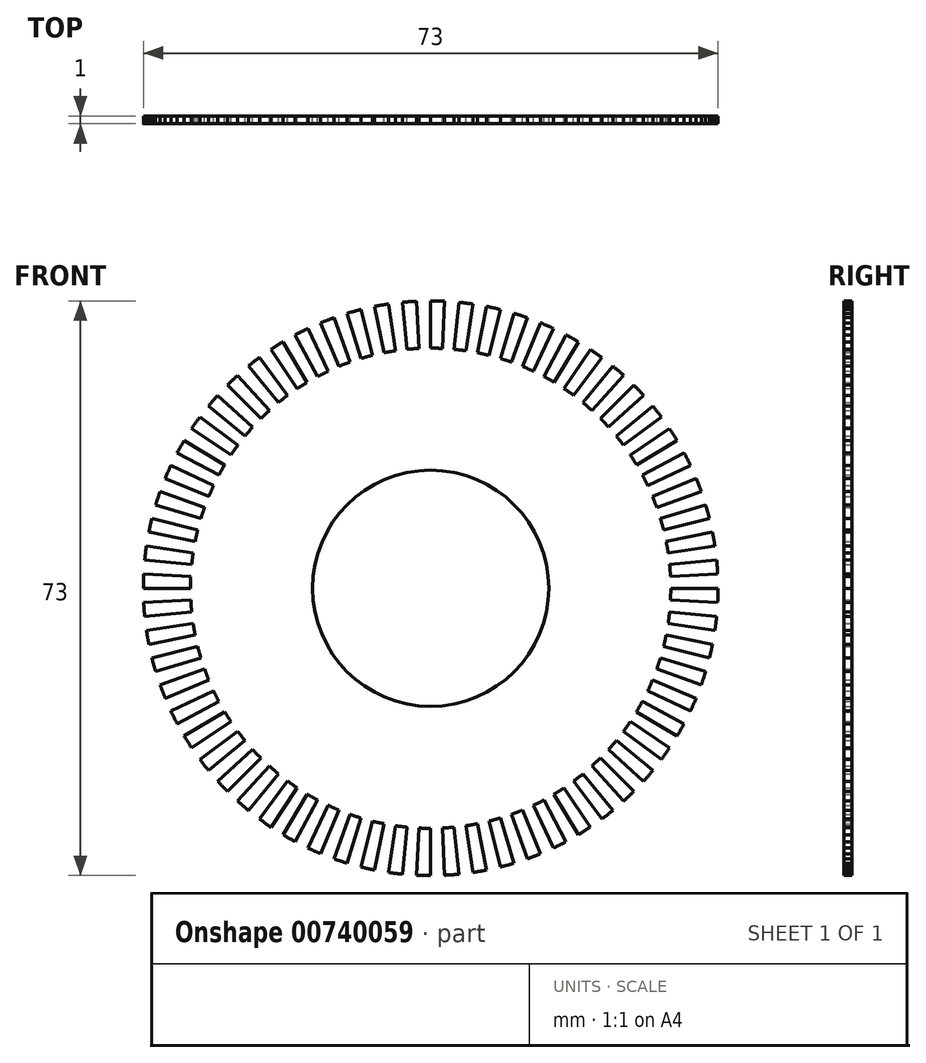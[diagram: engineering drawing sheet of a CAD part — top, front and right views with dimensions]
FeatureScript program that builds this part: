
annotation { "Feature Type Name" : "Feature", "Feature Type Description" : "" }
export const myFeature = defineFeature(function(context is Context, id is Id, definition is map)
    precondition{}
    {
        {
            var Q0;
            Q0=qCreatedBy(makeId("Front.planeOp"),FACE);
            var sketch = newSketch(context, id + "F0", { "sketchPlane" : qUnion([Q0])});
            skArc(sketch, "E0", {"start": v(1.8, 36.46) * mm, "mid": v(0.9, 36.49) * mm, "end": v(0, 36.5) * mm});
            skLineSegment(sketch, "E1", {"start": v(0, 30.5) * mm, "end": v(0, 36.5) * mm});
            skArc(sketch, "E2", {"start": v(1.5, 30.46) * mm, "mid": v(0.75, 30.5) * mm, "end": v(0, 30.5) * mm});
            skLineSegment(sketch, "E3", {"start": v(1.5, 30.46) * mm, "end": v(1.8, 36.46) * mm});
            skLineSegment(sketch, "E4.1.0", {"start": v(-1.5, 30.46) * mm, "end": v(-1.8, 36.46) * mm});
            skArc(sketch, "E4.1.1", {"start": v(-1.8, 36.46) * mm, "mid": v(-2.69, 36.4) * mm, "end": v(-3.58, 36.32) * mm});
            skArc(sketch, "E4.1.2", {"start": v(-1.5, 30.46) * mm, "mid": v(-2.24, 30.42) * mm, "end": v(-2.99, 30.35) * mm});
            skLineSegment(sketch, "E4.1.3", {"start": v(-2.99, 30.35) * mm, "end": v(-3.58, 36.32) * mm});
            skLineSegment(sketch, "E4.2.0", {"start": v(-4.48, 30.17) * mm, "end": v(-5.36, 36.1) * mm});
            skArc(sketch, "E4.2.1", {"start": v(-5.36, 36.1) * mm, "mid": v(-6.24, 35.96) * mm, "end": v(-7.12, 35.8) * mm});
            skArc(sketch, "E4.2.2", {"start": v(-4.48, 30.17) * mm, "mid": v(-5.21, 30.05) * mm, "end": v(-5.95, 29.91) * mm});
            skLineSegment(sketch, "E4.2.3", {"start": v(-5.95, 29.91) * mm, "end": v(-7.12, 35.8) * mm});
            skLineSegment(sketch, "E4.3.0", {"start": v(-7.41, 29.59) * mm, "end": v(-8.87, 35.4) * mm});
            skArc(sketch, "E4.3.1", {"start": v(-8.87, 35.4) * mm, "mid": v(-9.74, 35.18) * mm, "end": v(-10.6, 34.93) * mm});
            skArc(sketch, "E4.3.2", {"start": v(-7.41, 29.59) * mm, "mid": v(-8.13, 29.4) * mm, "end": v(-8.85, 29.19) * mm});
            skLineSegment(sketch, "E4.3.3", {"start": v(-8.85, 29.19) * mm, "end": v(-10.6, 34.93) * mm});
            skLineSegment(sketch, "E4.4.0", {"start": v(-10.28, 28.72) * mm, "end": v(-12.3, 34.37) * mm});
            skArc(sketch, "E4.4.1", {"start": v(-12.3, 34.37) * mm, "mid": v(-13.14, 34.05) * mm, "end": v(-13.97, 33.72) * mm});
            skArc(sketch, "E4.4.2", {"start": v(-10.28, 28.72) * mm, "mid": v(-10.98, 28.46) * mm, "end": v(-11.67, 28.18) * mm});
            skLineSegment(sketch, "E4.4.3", {"start": v(-11.67, 28.18) * mm, "end": v(-13.97, 33.72) * mm});
            skLineSegment(sketch, "E4.5.0", {"start": v(-13.04, 27.57) * mm, "end": v(-15.6, 33) * mm});
            skArc(sketch, "E4.5.1", {"start": v(-15.6, 33) * mm, "mid": v(-16.41, 32.6) * mm, "end": v(-17.2, 32.2) * mm});
            skArc(sketch, "E4.5.2", {"start": v(-13.04, 27.57) * mm, "mid": v(-13.71, 27.24) * mm, "end": v(-14.38, 26.9) * mm});
            skLineSegment(sketch, "E4.5.3", {"start": v(-14.38, 26.9) * mm, "end": v(-17.2, 32.2) * mm});
            skLineSegment(sketch, "E4.6.0", {"start": v(-15.68, 26.16) * mm, "end": v(-18.76, 31.3) * mm});
            skArc(sketch, "E4.6.1", {"start": v(-18.76, 31.3) * mm, "mid": v(-19.53, 30.84) * mm, "end": v(-20.28, 30.35) * mm});
            skArc(sketch, "E4.6.2", {"start": v(-15.68, 26.16) * mm, "mid": v(-16.32, 25.77) * mm, "end": v(-16.94, 25.36) * mm});
            skLineSegment(sketch, "E4.6.3", {"start": v(-16.94, 25.36) * mm, "end": v(-20.28, 30.35) * mm});
            skLineSegment(sketch, "E4.7.0", {"start": v(-18.17, 24.5) * mm, "end": v(-21.74, 29.32) * mm});
            skArc(sketch, "E4.7.1", {"start": v(-21.74, 29.32) * mm, "mid": v(-22.46, 28.77) * mm, "end": v(-23.16, 28.21) * mm});
            skArc(sketch, "E4.7.2", {"start": v(-18.17, 24.5) * mm, "mid": v(-18.76, 24.04) * mm, "end": v(-19.35, 23.58) * mm});
            skLineSegment(sketch, "E4.7.3", {"start": v(-19.35, 23.58) * mm, "end": v(-23.16, 28.21) * mm});
            skLineSegment(sketch, "E4.8.0", {"start": v(-20.48, 22.6) * mm, "end": v(-24.51, 27.04) * mm});
            skArc(sketch, "E4.8.1", {"start": v(-24.51, 27.04) * mm, "mid": v(-25.17, 26.44) * mm, "end": v(-25.8, 25.8) * mm});
            skArc(sketch, "E4.8.2", {"start": v(-20.48, 22.6) * mm, "mid": v(-21.03, 22.09) * mm, "end": v(-21.57, 21.57) * mm});
            skLineSegment(sketch, "E4.8.3", {"start": v(-21.57, 21.57) * mm, "end": v(-25.8, 25.8) * mm});
            skLineSegment(sketch, "E4.9.0", {"start": v(-22.6, 20.48) * mm, "end": v(-27.04, 24.51) * mm});
            skArc(sketch, "E4.9.1", {"start": v(-27.04, 24.51) * mm, "mid": v(-27.64, 23.84) * mm, "end": v(-28.21, 23.16) * mm});
            skArc(sketch, "E4.9.2", {"start": v(-22.6, 20.48) * mm, "mid": v(-23.1, 19.92) * mm, "end": v(-23.58, 19.35) * mm});
            skLineSegment(sketch, "E4.9.3", {"start": v(-23.58, 19.35) * mm, "end": v(-28.21, 23.16) * mm});
            skLineSegment(sketch, "E4.10.0", {"start": v(-24.5, 18.17) * mm, "end": v(-29.32, 21.74) * mm});
            skArc(sketch, "E4.10.1", {"start": v(-29.32, 21.74) * mm, "mid": v(-29.84, 21.02) * mm, "end": v(-30.35, 20.28) * mm});
            skArc(sketch, "E4.10.2", {"start": v(-24.5, 18.17) * mm, "mid": v(-24.94, 17.56) * mm, "end": v(-25.36, 16.94) * mm});
            skLineSegment(sketch, "E4.10.3", {"start": v(-25.36, 16.94) * mm, "end": v(-30.35, 20.28) * mm});
            skLineSegment(sketch, "E4.11.0", {"start": v(-26.16, 15.68) * mm, "end": v(-31.3, 18.76) * mm});
            skArc(sketch, "E4.11.1", {"start": v(-31.3, 18.76) * mm, "mid": v(-31.76, 18) * mm, "end": v(-32.2, 17.2) * mm});
            skArc(sketch, "E4.11.2", {"start": v(-26.16, 15.68) * mm, "mid": v(-26.54, 15.03) * mm, "end": v(-26.9, 14.38) * mm});
            skLineSegment(sketch, "E4.11.3", {"start": v(-26.9, 14.38) * mm, "end": v(-32.2, 17.2) * mm});
            skLineSegment(sketch, "E4.12.0", {"start": v(-27.57, 13.04) * mm, "end": v(-33, 15.6) * mm});
            skArc(sketch, "E4.12.1", {"start": v(-33, 15.6) * mm, "mid": v(-33.37, 14.8) * mm, "end": v(-33.72, 13.97) * mm});
            skArc(sketch, "E4.12.2", {"start": v(-27.57, 13.04) * mm, "mid": v(-27.88, 12.36) * mm, "end": v(-28.18, 11.67) * mm});
            skLineSegment(sketch, "E4.12.3", {"start": v(-28.18, 11.67) * mm, "end": v(-33.72, 13.97) * mm});
            skLineSegment(sketch, "E4.13.0", {"start": v(-28.72, 10.28) * mm, "end": v(-34.37, 12.3) * mm});
            skArc(sketch, "E4.13.1", {"start": v(-34.37, 12.3) * mm, "mid": v(-34.66, 11.45) * mm, "end": v(-34.93, 10.6) * mm});
            skArc(sketch, "E4.13.2", {"start": v(-28.72, 10.28) * mm, "mid": v(-28.96, 9.57) * mm, "end": v(-29.19, 8.85) * mm});
            skLineSegment(sketch, "E4.13.3", {"start": v(-29.19, 8.85) * mm, "end": v(-34.93, 10.6) * mm});
            skLineSegment(sketch, "E4.14.0", {"start": v(-29.59, 7.41) * mm, "end": v(-35.4, 8.87) * mm});
            skArc(sketch, "E4.14.1", {"start": v(-35.4, 8.87) * mm, "mid": v(-35.61, 8) * mm, "end": v(-35.8, 7.12) * mm});
            skArc(sketch, "E4.14.2", {"start": v(-29.59, 7.41) * mm, "mid": v(-29.76, 6.68) * mm, "end": v(-29.91, 5.95) * mm});
            skLineSegment(sketch, "E4.14.3", {"start": v(-29.91, 5.95) * mm, "end": v(-35.8, 7.12) * mm});
            skLineSegment(sketch, "E4.15.0", {"start": v(-30.17, 4.48) * mm, "end": v(-36.1, 5.36) * mm});
            skArc(sketch, "E4.15.1", {"start": v(-36.1, 5.36) * mm, "mid": v(-36.23, 4.47) * mm, "end": v(-36.32, 3.58) * mm});
            skArc(sketch, "E4.15.2", {"start": v(-30.17, 4.48) * mm, "mid": v(-30.27, 3.73) * mm, "end": v(-30.35, 2.99) * mm});
            skLineSegment(sketch, "E4.15.3", {"start": v(-30.35, 2.99) * mm, "end": v(-36.32, 3.58) * mm});
            skLineSegment(sketch, "E4.16.0", {"start": v(-30.46, 1.5) * mm, "end": v(-36.46, 1.8) * mm});
            skArc(sketch, "E4.16.1", {"start": v(-36.46, 1.8) * mm, "mid": v(-36.49, 0.9) * mm, "end": v(-36.5, 0) * mm});
            skArc(sketch, "E4.16.2", {"start": v(-30.46, 1.5) * mm, "mid": v(-30.5, 0.75) * mm, "end": v(-30.5, 0) * mm});
            skLineSegment(sketch, "E4.16.3", {"start": v(-30.5, 0) * mm, "end": v(-36.5, 0) * mm});
            skLineSegment(sketch, "E4.17.0", {"start": v(-30.46, -1.5) * mm, "end": v(-36.46, -1.8) * mm});
            skArc(sketch, "E4.17.1", {"start": v(-36.46, -1.8) * mm, "mid": v(-36.4, -2.69) * mm, "end": v(-36.32, -3.58) * mm});
            skArc(sketch, "E4.17.2", {"start": v(-30.46, -1.5) * mm, "mid": v(-30.42, -2.24) * mm, "end": v(-30.35, -2.99) * mm});
            skLineSegment(sketch, "E4.17.3", {"start": v(-30.35, -2.99) * mm, "end": v(-36.32, -3.58) * mm});
            skLineSegment(sketch, "E4.18.0", {"start": v(-30.17, -4.48) * mm, "end": v(-36.1, -5.36) * mm});
            skArc(sketch, "E4.18.1", {"start": v(-36.1, -5.36) * mm, "mid": v(-35.96, -6.24) * mm, "end": v(-35.8, -7.12) * mm});
            skArc(sketch, "E4.18.2", {"start": v(-30.17, -4.48) * mm, "mid": v(-30.05, -5.21) * mm, "end": v(-29.91, -5.95) * mm});
            skLineSegment(sketch, "E4.18.3", {"start": v(-29.91, -5.95) * mm, "end": v(-35.8, -7.12) * mm});
            skLineSegment(sketch, "E4.19.0", {"start": v(-29.59, -7.41) * mm, "end": v(-35.4, -8.87) * mm});
            skArc(sketch, "E4.19.1", {"start": v(-35.4, -8.87) * mm, "mid": v(-35.18, -9.74) * mm, "end": v(-34.93, -10.6) * mm});
            skArc(sketch, "E4.19.2", {"start": v(-29.59, -7.41) * mm, "mid": v(-29.4, -8.13) * mm, "end": v(-29.19, -8.85) * mm});
            skLineSegment(sketch, "E4.19.3", {"start": v(-29.19, -8.85) * mm, "end": v(-34.93, -10.6) * mm});
            skLineSegment(sketch, "E4.20.0", {"start": v(-28.72, -10.28) * mm, "end": v(-34.37, -12.3) * mm});
            skArc(sketch, "E4.20.1", {"start": v(-34.37, -12.3) * mm, "mid": v(-34.05, -13.14) * mm, "end": v(-33.72, -13.97) * mm});
            skArc(sketch, "E4.20.2", {"start": v(-28.72, -10.28) * mm, "mid": v(-28.46, -10.98) * mm, "end": v(-28.18, -11.67) * mm});
            skLineSegment(sketch, "E4.20.3", {"start": v(-28.18, -11.67) * mm, "end": v(-33.72, -13.97) * mm});
            skLineSegment(sketch, "E4.21.0", {"start": v(-27.57, -13.04) * mm, "end": v(-33, -15.6) * mm});
            skArc(sketch, "E4.21.1", {"start": v(-33, -15.6) * mm, "mid": v(-32.6, -16.41) * mm, "end": v(-32.2, -17.2) * mm});
            skArc(sketch, "E4.21.2", {"start": v(-27.57, -13.04) * mm, "mid": v(-27.24, -13.71) * mm, "end": v(-26.9, -14.38) * mm});
            skLineSegment(sketch, "E4.21.3", {"start": v(-26.9, -14.38) * mm, "end": v(-32.2, -17.2) * mm});
            skLineSegment(sketch, "E4.22.0", {"start": v(-26.16, -15.68) * mm, "end": v(-31.3, -18.76) * mm});
            skArc(sketch, "E4.22.1", {"start": v(-31.3, -18.76) * mm, "mid": v(-30.84, -19.53) * mm, "end": v(-30.35, -20.28) * mm});
            skArc(sketch, "E4.22.2", {"start": v(-26.16, -15.68) * mm, "mid": v(-25.77, -16.32) * mm, "end": v(-25.36, -16.94) * mm});
            skLineSegment(sketch, "E4.22.3", {"start": v(-25.36, -16.94) * mm, "end": v(-30.35, -20.28) * mm});
            skLineSegment(sketch, "E4.23.0", {"start": v(-24.5, -18.17) * mm, "end": v(-29.32, -21.74) * mm});
            skArc(sketch, "E4.23.1", {"start": v(-29.32, -21.74) * mm, "mid": v(-28.77, -22.46) * mm, "end": v(-28.21, -23.16) * mm});
            skArc(sketch, "E4.23.2", {"start": v(-24.5, -18.17) * mm, "mid": v(-24.04, -18.76) * mm, "end": v(-23.58, -19.35) * mm});
            skLineSegment(sketch, "E4.23.3", {"start": v(-23.58, -19.35) * mm, "end": v(-28.21, -23.16) * mm});
            skLineSegment(sketch, "E4.24.0", {"start": v(-22.6, -20.48) * mm, "end": v(-27.04, -24.51) * mm});
            skArc(sketch, "E4.24.1", {"start": v(-27.04, -24.51) * mm, "mid": v(-26.44, -25.17) * mm, "end": v(-25.8, -25.8) * mm});
            skArc(sketch, "E4.24.2", {"start": v(-22.6, -20.48) * mm, "mid": v(-22.09, -21.03) * mm, "end": v(-21.57, -21.57) * mm});
            skLineSegment(sketch, "E4.24.3", {"start": v(-21.57, -21.57) * mm, "end": v(-25.8, -25.8) * mm});
            skLineSegment(sketch, "E4.25.0", {"start": v(-20.48, -22.6) * mm, "end": v(-24.51, -27.04) * mm});
            skArc(sketch, "E4.25.1", {"start": v(-24.51, -27.04) * mm, "mid": v(-23.84, -27.64) * mm, "end": v(-23.16, -28.21) * mm});
            skArc(sketch, "E4.25.2", {"start": v(-20.48, -22.6) * mm, "mid": v(-19.92, -23.1) * mm, "end": v(-19.35, -23.58) * mm});
            skLineSegment(sketch, "E4.25.3", {"start": v(-19.35, -23.58) * mm, "end": v(-23.16, -28.21) * mm});
            skLineSegment(sketch, "E4.26.0", {"start": v(-18.17, -24.5) * mm, "end": v(-21.74, -29.32) * mm});
            skArc(sketch, "E4.26.1", {"start": v(-21.74, -29.32) * mm, "mid": v(-21.02, -29.84) * mm, "end": v(-20.28, -30.35) * mm});
            skArc(sketch, "E4.26.2", {"start": v(-18.17, -24.5) * mm, "mid": v(-17.56, -24.94) * mm, "end": v(-16.94, -25.36) * mm});
            skLineSegment(sketch, "E4.26.3", {"start": v(-16.94, -25.36) * mm, "end": v(-20.28, -30.35) * mm});
            skLineSegment(sketch, "E4.27.0", {"start": v(-15.68, -26.16) * mm, "end": v(-18.76, -31.3) * mm});
            skArc(sketch, "E4.27.1", {"start": v(-18.76, -31.3) * mm, "mid": v(-18, -31.76) * mm, "end": v(-17.2, -32.2) * mm});
            skArc(sketch, "E4.27.2", {"start": v(-15.68, -26.16) * mm, "mid": v(-15.03, -26.54) * mm, "end": v(-14.38, -26.9) * mm});
            skLineSegment(sketch, "E4.27.3", {"start": v(-14.38, -26.9) * mm, "end": v(-17.2, -32.2) * mm});
            skLineSegment(sketch, "E4.28.0", {"start": v(-13.04, -27.57) * mm, "end": v(-15.6, -33) * mm});
            skArc(sketch, "E4.28.1", {"start": v(-15.6, -33) * mm, "mid": v(-14.8, -33.37) * mm, "end": v(-13.97, -33.72) * mm});
            skArc(sketch, "E4.28.2", {"start": v(-13.04, -27.57) * mm, "mid": v(-12.36, -27.88) * mm, "end": v(-11.67, -28.18) * mm});
            skLineSegment(sketch, "E4.28.3", {"start": v(-11.67, -28.18) * mm, "end": v(-13.97, -33.72) * mm});
            skLineSegment(sketch, "E4.29.0", {"start": v(-10.28, -28.72) * mm, "end": v(-12.3, -34.37) * mm});
            skArc(sketch, "E4.29.1", {"start": v(-12.3, -34.37) * mm, "mid": v(-11.45, -34.66) * mm, "end": v(-10.6, -34.93) * mm});
            skArc(sketch, "E4.29.2", {"start": v(-10.28, -28.72) * mm, "mid": v(-9.57, -28.96) * mm, "end": v(-8.85, -29.19) * mm});
            skLineSegment(sketch, "E4.29.3", {"start": v(-8.85, -29.19) * mm, "end": v(-10.6, -34.93) * mm});
            skLineSegment(sketch, "E4.30.0", {"start": v(-7.41, -29.59) * mm, "end": v(-8.87, -35.4) * mm});
            skArc(sketch, "E4.30.1", {"start": v(-8.87, -35.4) * mm, "mid": v(-8, -35.61) * mm, "end": v(-7.12, -35.8) * mm});
            skArc(sketch, "E4.30.2", {"start": v(-7.41, -29.59) * mm, "mid": v(-6.68, -29.76) * mm, "end": v(-5.95, -29.91) * mm});
            skLineSegment(sketch, "E4.30.3", {"start": v(-5.95, -29.91) * mm, "end": v(-7.12, -35.8) * mm});
            skLineSegment(sketch, "E4.31.0", {"start": v(-4.48, -30.17) * mm, "end": v(-5.36, -36.1) * mm});
            skArc(sketch, "E4.31.1", {"start": v(-5.36, -36.1) * mm, "mid": v(-4.47, -36.23) * mm, "end": v(-3.58, -36.32) * mm});
            skArc(sketch, "E4.31.2", {"start": v(-4.48, -30.17) * mm, "mid": v(-3.73, -30.27) * mm, "end": v(-2.99, -30.35) * mm});
            skLineSegment(sketch, "E4.31.3", {"start": v(-2.99, -30.35) * mm, "end": v(-3.58, -36.32) * mm});
            skLineSegment(sketch, "E4.32.0", {"start": v(-1.5, -30.46) * mm, "end": v(-1.8, -36.46) * mm});
            skArc(sketch, "E4.32.1", {"start": v(-1.8, -36.46) * mm, "mid": v(-0.9, -36.49) * mm, "end": v(0, -36.5) * mm});
            skArc(sketch, "E4.32.2", {"start": v(-1.5, -30.46) * mm, "mid": v(-0.75, -30.5) * mm, "end": v(0, -30.5) * mm});
            skLineSegment(sketch, "E4.32.3", {"start": v(0, -30.5) * mm, "end": v(0, -36.5) * mm});
            skLineSegment(sketch, "E4.33.0", {"start": v(1.5, -30.46) * mm, "end": v(1.8, -36.46) * mm});
            skArc(sketch, "E4.33.1", {"start": v(1.8, -36.46) * mm, "mid": v(2.69, -36.4) * mm, "end": v(3.58, -36.32) * mm});
            skArc(sketch, "E4.33.2", {"start": v(1.5, -30.46) * mm, "mid": v(2.24, -30.42) * mm, "end": v(2.99, -30.35) * mm});
            skLineSegment(sketch, "E4.33.3", {"start": v(2.99, -30.35) * mm, "end": v(3.58, -36.32) * mm});
            skLineSegment(sketch, "E4.34.0", {"start": v(4.48, -30.17) * mm, "end": v(5.36, -36.1) * mm});
            skArc(sketch, "E4.34.1", {"start": v(5.36, -36.1) * mm, "mid": v(6.24, -35.96) * mm, "end": v(7.12, -35.8) * mm});
            skArc(sketch, "E4.34.2", {"start": v(4.48, -30.17) * mm, "mid": v(5.21, -30.05) * mm, "end": v(5.95, -29.91) * mm});
            skLineSegment(sketch, "E4.34.3", {"start": v(5.95, -29.91) * mm, "end": v(7.12, -35.8) * mm});
            skLineSegment(sketch, "E4.35.0", {"start": v(7.41, -29.59) * mm, "end": v(8.87, -35.4) * mm});
            skArc(sketch, "E4.35.1", {"start": v(8.87, -35.4) * mm, "mid": v(9.74, -35.18) * mm, "end": v(10.6, -34.93) * mm});
            skArc(sketch, "E4.35.2", {"start": v(7.41, -29.59) * mm, "mid": v(8.13, -29.4) * mm, "end": v(8.85, -29.19) * mm});
            skLineSegment(sketch, "E4.35.3", {"start": v(8.85, -29.19) * mm, "end": v(10.6, -34.93) * mm});
            skLineSegment(sketch, "E4.36.0", {"start": v(10.28, -28.72) * mm, "end": v(12.3, -34.37) * mm});
            skArc(sketch, "E4.36.1", {"start": v(12.3, -34.37) * mm, "mid": v(13.14, -34.05) * mm, "end": v(13.97, -33.72) * mm});
            skArc(sketch, "E4.36.2", {"start": v(10.28, -28.72) * mm, "mid": v(10.98, -28.46) * mm, "end": v(11.67, -28.18) * mm});
            skLineSegment(sketch, "E4.36.3", {"start": v(11.67, -28.18) * mm, "end": v(13.97, -33.72) * mm});
            skLineSegment(sketch, "E4.37.0", {"start": v(13.04, -27.57) * mm, "end": v(15.6, -33) * mm});
            skArc(sketch, "E4.37.1", {"start": v(15.6, -33) * mm, "mid": v(16.41, -32.6) * mm, "end": v(17.2, -32.2) * mm});
            skArc(sketch, "E4.37.2", {"start": v(13.04, -27.57) * mm, "mid": v(13.71, -27.24) * mm, "end": v(14.38, -26.9) * mm});
            skLineSegment(sketch, "E4.37.3", {"start": v(14.38, -26.9) * mm, "end": v(17.2, -32.2) * mm});
            skLineSegment(sketch, "E4.38.0", {"start": v(15.68, -26.16) * mm, "end": v(18.76, -31.3) * mm});
            skArc(sketch, "E4.38.1", {"start": v(18.76, -31.3) * mm, "mid": v(19.53, -30.84) * mm, "end": v(20.28, -30.35) * mm});
            skArc(sketch, "E4.38.2", {"start": v(15.68, -26.16) * mm, "mid": v(16.32, -25.77) * mm, "end": v(16.94, -25.36) * mm});
            skLineSegment(sketch, "E4.38.3", {"start": v(16.94, -25.36) * mm, "end": v(20.28, -30.35) * mm});
            skLineSegment(sketch, "E4.39.0", {"start": v(18.17, -24.5) * mm, "end": v(21.74, -29.32) * mm});
            skArc(sketch, "E4.39.1", {"start": v(21.74, -29.32) * mm, "mid": v(22.46, -28.77) * mm, "end": v(23.16, -28.21) * mm});
            skArc(sketch, "E4.39.2", {"start": v(18.17, -24.5) * mm, "mid": v(18.76, -24.04) * mm, "end": v(19.35, -23.58) * mm});
            skLineSegment(sketch, "E4.39.3", {"start": v(19.35, -23.58) * mm, "end": v(23.16, -28.21) * mm});
            skLineSegment(sketch, "E4.40.0", {"start": v(20.48, -22.6) * mm, "end": v(24.51, -27.04) * mm});
            skArc(sketch, "E4.40.1", {"start": v(24.51, -27.04) * mm, "mid": v(25.17, -26.44) * mm, "end": v(25.8, -25.8) * mm});
            skArc(sketch, "E4.40.2", {"start": v(20.48, -22.6) * mm, "mid": v(21.03, -22.09) * mm, "end": v(21.57, -21.57) * mm});
            skLineSegment(sketch, "E4.40.3", {"start": v(21.57, -21.57) * mm, "end": v(25.8, -25.8) * mm});
            skLineSegment(sketch, "E4.41.0", {"start": v(22.6, -20.48) * mm, "end": v(27.04, -24.51) * mm});
            skArc(sketch, "E4.41.1", {"start": v(27.04, -24.51) * mm, "mid": v(27.64, -23.84) * mm, "end": v(28.21, -23.16) * mm});
            skArc(sketch, "E4.41.2", {"start": v(22.6, -20.48) * mm, "mid": v(23.1, -19.92) * mm, "end": v(23.58, -19.35) * mm});
            skLineSegment(sketch, "E4.41.3", {"start": v(23.58, -19.35) * mm, "end": v(28.21, -23.16) * mm});
            skLineSegment(sketch, "E4.42.0", {"start": v(24.5, -18.17) * mm, "end": v(29.32, -21.74) * mm});
            skArc(sketch, "E4.42.1", {"start": v(29.32, -21.74) * mm, "mid": v(29.84, -21.02) * mm, "end": v(30.35, -20.28) * mm});
            skArc(sketch, "E4.42.2", {"start": v(24.5, -18.17) * mm, "mid": v(24.94, -17.56) * mm, "end": v(25.36, -16.94) * mm});
            skLineSegment(sketch, "E4.42.3", {"start": v(25.36, -16.94) * mm, "end": v(30.35, -20.28) * mm});
            skLineSegment(sketch, "E4.43.0", {"start": v(26.16, -15.68) * mm, "end": v(31.3, -18.76) * mm});
            skArc(sketch, "E4.43.1", {"start": v(31.3, -18.76) * mm, "mid": v(31.76, -18) * mm, "end": v(32.2, -17.2) * mm});
            skArc(sketch, "E4.43.2", {"start": v(26.16, -15.68) * mm, "mid": v(26.54, -15.03) * mm, "end": v(26.9, -14.38) * mm});
            skLineSegment(sketch, "E4.43.3", {"start": v(26.9, -14.38) * mm, "end": v(32.2, -17.2) * mm});
            skLineSegment(sketch, "E4.44.0", {"start": v(27.57, -13.04) * mm, "end": v(33, -15.6) * mm});
            skArc(sketch, "E4.44.1", {"start": v(33, -15.6) * mm, "mid": v(33.37, -14.8) * mm, "end": v(33.72, -13.97) * mm});
            skArc(sketch, "E4.44.2", {"start": v(27.57, -13.04) * mm, "mid": v(27.88, -12.36) * mm, "end": v(28.18, -11.67) * mm});
            skLineSegment(sketch, "E4.44.3", {"start": v(28.18, -11.67) * mm, "end": v(33.72, -13.97) * mm});
            skLineSegment(sketch, "E4.45.0", {"start": v(28.72, -10.28) * mm, "end": v(34.37, -12.3) * mm});
            skArc(sketch, "E4.45.1", {"start": v(34.37, -12.3) * mm, "mid": v(34.66, -11.45) * mm, "end": v(34.93, -10.6) * mm});
            skArc(sketch, "E4.45.2", {"start": v(28.72, -10.28) * mm, "mid": v(28.96, -9.57) * mm, "end": v(29.19, -8.85) * mm});
            skLineSegment(sketch, "E4.45.3", {"start": v(29.19, -8.85) * mm, "end": v(34.93, -10.6) * mm});
            skLineSegment(sketch, "E4.46.0", {"start": v(29.59, -7.41) * mm, "end": v(35.4, -8.87) * mm});
            skArc(sketch, "E4.46.1", {"start": v(35.4, -8.87) * mm, "mid": v(35.61, -8) * mm, "end": v(35.8, -7.12) * mm});
            skArc(sketch, "E4.46.2", {"start": v(29.59, -7.41) * mm, "mid": v(29.76, -6.68) * mm, "end": v(29.91, -5.95) * mm});
            skLineSegment(sketch, "E4.46.3", {"start": v(29.91, -5.95) * mm, "end": v(35.8, -7.12) * mm});
            skLineSegment(sketch, "E4.47.0", {"start": v(30.17, -4.48) * mm, "end": v(36.1, -5.36) * mm});
            skArc(sketch, "E4.47.1", {"start": v(36.1, -5.36) * mm, "mid": v(36.23, -4.47) * mm, "end": v(36.32, -3.58) * mm});
            skArc(sketch, "E4.47.2", {"start": v(30.17, -4.48) * mm, "mid": v(30.27, -3.73) * mm, "end": v(30.35, -2.99) * mm});
            skLineSegment(sketch, "E4.47.3", {"start": v(30.35, -2.99) * mm, "end": v(36.32, -3.58) * mm});
            skLineSegment(sketch, "E4.48.0", {"start": v(30.46, -1.5) * mm, "end": v(36.46, -1.8) * mm});
            skArc(sketch, "E4.48.1", {"start": v(36.46, -1.8) * mm, "mid": v(36.49, -0.9) * mm, "end": v(36.5, 0) * mm});
            skArc(sketch, "E4.48.2", {"start": v(30.46, -1.5) * mm, "mid": v(30.5, -0.75) * mm, "end": v(30.5, 0) * mm});
            skLineSegment(sketch, "E4.48.3", {"start": v(30.5, 0) * mm, "end": v(36.5, 0) * mm});
            skLineSegment(sketch, "E4.49.0", {"start": v(30.46, 1.5) * mm, "end": v(36.46, 1.8) * mm});
            skArc(sketch, "E4.49.1", {"start": v(36.46, 1.8) * mm, "mid": v(36.4, 2.69) * mm, "end": v(36.32, 3.58) * mm});
            skArc(sketch, "E4.49.2", {"start": v(30.46, 1.5) * mm, "mid": v(30.42, 2.24) * mm, "end": v(30.35, 2.99) * mm});
            skLineSegment(sketch, "E4.49.3", {"start": v(30.35, 2.99) * mm, "end": v(36.32, 3.58) * mm});
            skLineSegment(sketch, "E4.50.0", {"start": v(30.17, 4.48) * mm, "end": v(36.1, 5.36) * mm});
            skArc(sketch, "E4.50.1", {"start": v(36.1, 5.36) * mm, "mid": v(35.96, 6.24) * mm, "end": v(35.8, 7.12) * mm});
            skArc(sketch, "E4.50.2", {"start": v(30.17, 4.48) * mm, "mid": v(30.05, 5.21) * mm, "end": v(29.91, 5.95) * mm});
            skLineSegment(sketch, "E4.50.3", {"start": v(29.91, 5.95) * mm, "end": v(35.8, 7.12) * mm});
            skLineSegment(sketch, "E4.51.0", {"start": v(29.59, 7.41) * mm, "end": v(35.4, 8.87) * mm});
            skArc(sketch, "E4.51.1", {"start": v(35.4, 8.87) * mm, "mid": v(35.18, 9.74) * mm, "end": v(34.93, 10.6) * mm});
            skArc(sketch, "E4.51.2", {"start": v(29.59, 7.41) * mm, "mid": v(29.4, 8.13) * mm, "end": v(29.19, 8.85) * mm});
            skLineSegment(sketch, "E4.51.3", {"start": v(29.19, 8.85) * mm, "end": v(34.93, 10.6) * mm});
            skLineSegment(sketch, "E4.52.0", {"start": v(28.72, 10.28) * mm, "end": v(34.37, 12.3) * mm});
            skArc(sketch, "E4.52.1", {"start": v(34.37, 12.3) * mm, "mid": v(34.05, 13.14) * mm, "end": v(33.72, 13.97) * mm});
            skArc(sketch, "E4.52.2", {"start": v(28.72, 10.28) * mm, "mid": v(28.46, 10.98) * mm, "end": v(28.18, 11.67) * mm});
            skLineSegment(sketch, "E4.52.3", {"start": v(28.18, 11.67) * mm, "end": v(33.72, 13.97) * mm});
            skLineSegment(sketch, "E4.53.0", {"start": v(27.57, 13.04) * mm, "end": v(33, 15.6) * mm});
            skArc(sketch, "E4.53.1", {"start": v(33, 15.6) * mm, "mid": v(32.6, 16.41) * mm, "end": v(32.2, 17.2) * mm});
            skArc(sketch, "E4.53.2", {"start": v(27.57, 13.04) * mm, "mid": v(27.24, 13.71) * mm, "end": v(26.9, 14.38) * mm});
            skLineSegment(sketch, "E4.53.3", {"start": v(26.9, 14.38) * mm, "end": v(32.2, 17.2) * mm});
            skLineSegment(sketch, "E4.54.0", {"start": v(26.16, 15.68) * mm, "end": v(31.3, 18.76) * mm});
            skArc(sketch, "E4.54.1", {"start": v(31.3, 18.76) * mm, "mid": v(30.84, 19.53) * mm, "end": v(30.35, 20.28) * mm});
            skArc(sketch, "E4.54.2", {"start": v(26.16, 15.68) * mm, "mid": v(25.77, 16.32) * mm, "end": v(25.36, 16.94) * mm});
            skLineSegment(sketch, "E4.54.3", {"start": v(25.36, 16.94) * mm, "end": v(30.35, 20.28) * mm});
            skLineSegment(sketch, "E4.55.0", {"start": v(24.5, 18.17) * mm, "end": v(29.32, 21.74) * mm});
            skArc(sketch, "E4.55.1", {"start": v(29.32, 21.74) * mm, "mid": v(28.77, 22.46) * mm, "end": v(28.21, 23.16) * mm});
            skArc(sketch, "E4.55.2", {"start": v(24.5, 18.17) * mm, "mid": v(24.04, 18.76) * mm, "end": v(23.58, 19.35) * mm});
            skLineSegment(sketch, "E4.55.3", {"start": v(23.58, 19.35) * mm, "end": v(28.21, 23.16) * mm});
            skLineSegment(sketch, "E4.56.0", {"start": v(22.6, 20.48) * mm, "end": v(27.04, 24.51) * mm});
            skArc(sketch, "E4.56.1", {"start": v(27.04, 24.51) * mm, "mid": v(26.44, 25.17) * mm, "end": v(25.8, 25.8) * mm});
            skArc(sketch, "E4.56.2", {"start": v(22.6, 20.48) * mm, "mid": v(22.09, 21.03) * mm, "end": v(21.57, 21.57) * mm});
            skLineSegment(sketch, "E4.56.3", {"start": v(21.57, 21.57) * mm, "end": v(25.8, 25.8) * mm});
            skLineSegment(sketch, "E4.57.0", {"start": v(20.48, 22.6) * mm, "end": v(24.51, 27.04) * mm});
            skArc(sketch, "E4.57.1", {"start": v(24.51, 27.04) * mm, "mid": v(23.84, 27.64) * mm, "end": v(23.16, 28.21) * mm});
            skArc(sketch, "E4.57.2", {"start": v(20.48, 22.6) * mm, "mid": v(19.92, 23.1) * mm, "end": v(19.35, 23.58) * mm});
            skLineSegment(sketch, "E4.57.3", {"start": v(19.35, 23.58) * mm, "end": v(23.16, 28.21) * mm});
            skLineSegment(sketch, "E4.58.0", {"start": v(18.17, 24.5) * mm, "end": v(21.74, 29.32) * mm});
            skArc(sketch, "E4.58.1", {"start": v(21.74, 29.32) * mm, "mid": v(21.02, 29.84) * mm, "end": v(20.28, 30.35) * mm});
            skArc(sketch, "E4.58.2", {"start": v(18.17, 24.5) * mm, "mid": v(17.56, 24.94) * mm, "end": v(16.94, 25.36) * mm});
            skLineSegment(sketch, "E4.58.3", {"start": v(16.94, 25.36) * mm, "end": v(20.28, 30.35) * mm});
            skLineSegment(sketch, "E4.59.0", {"start": v(15.68, 26.16) * mm, "end": v(18.76, 31.3) * mm});
            skArc(sketch, "E4.59.1", {"start": v(18.76, 31.3) * mm, "mid": v(18, 31.76) * mm, "end": v(17.2, 32.2) * mm});
            skArc(sketch, "E4.59.2", {"start": v(15.68, 26.16) * mm, "mid": v(15.03, 26.54) * mm, "end": v(14.38, 26.9) * mm});
            skLineSegment(sketch, "E4.59.3", {"start": v(14.38, 26.9) * mm, "end": v(17.2, 32.2) * mm});
            skLineSegment(sketch, "E4.60.0", {"start": v(13.04, 27.57) * mm, "end": v(15.6, 33) * mm});
            skArc(sketch, "E4.60.1", {"start": v(15.6, 33) * mm, "mid": v(14.8, 33.37) * mm, "end": v(13.97, 33.72) * mm});
            skArc(sketch, "E4.60.2", {"start": v(13.04, 27.57) * mm, "mid": v(12.36, 27.88) * mm, "end": v(11.67, 28.18) * mm});
            skLineSegment(sketch, "E4.60.3", {"start": v(11.67, 28.18) * mm, "end": v(13.97, 33.72) * mm});
            skLineSegment(sketch, "E4.61.0", {"start": v(10.28, 28.72) * mm, "end": v(12.3, 34.37) * mm});
            skArc(sketch, "E4.61.1", {"start": v(12.3, 34.37) * mm, "mid": v(11.45, 34.66) * mm, "end": v(10.6, 34.93) * mm});
            skArc(sketch, "E4.61.2", {"start": v(10.28, 28.72) * mm, "mid": v(9.57, 28.96) * mm, "end": v(8.85, 29.19) * mm});
            skLineSegment(sketch, "E4.61.3", {"start": v(8.85, 29.19) * mm, "end": v(10.6, 34.93) * mm});
            skLineSegment(sketch, "E4.62.0", {"start": v(7.41, 29.59) * mm, "end": v(8.87, 35.4) * mm});
            skArc(sketch, "E4.62.1", {"start": v(8.87, 35.4) * mm, "mid": v(8, 35.61) * mm, "end": v(7.12, 35.8) * mm});
            skArc(sketch, "E4.62.2", {"start": v(7.41, 29.59) * mm, "mid": v(6.68, 29.76) * mm, "end": v(5.95, 29.91) * mm});
            skLineSegment(sketch, "E4.62.3", {"start": v(5.95, 29.91) * mm, "end": v(7.12, 35.8) * mm});
            skLineSegment(sketch, "E4.63.0", {"start": v(4.48, 30.17) * mm, "end": v(5.36, 36.1) * mm});
            skArc(sketch, "E4.63.1", {"start": v(5.36, 36.1) * mm, "mid": v(4.47, 36.23) * mm, "end": v(3.58, 36.32) * mm});
            skArc(sketch, "E4.63.2", {"start": v(4.48, 30.17) * mm, "mid": v(3.73, 30.27) * mm, "end": v(2.99, 30.35) * mm});
            skLineSegment(sketch, "E4.63.3", {"start": v(2.99, 30.35) * mm, "end": v(3.58, 36.32) * mm});
            skCircle(sketch, "E5", {"center": v(0, 0) * mm, "radius": 15 * mm});
            skSolve(sketch);
        }
        {
            var Q0;
            Q0 = qSketchRegion(id + "F0", true);
            extrude(context, id + "F1", {"entities" : qUnion([Q0]), "depth" : 1 * mm, "offsetDistance" : 25 * mm});
        }
    });
